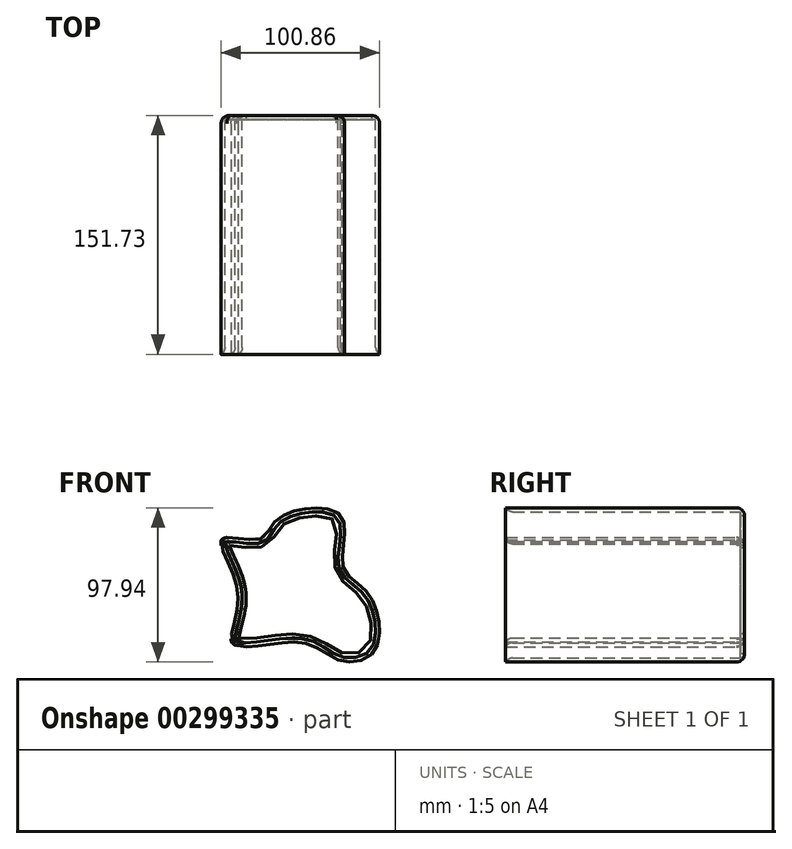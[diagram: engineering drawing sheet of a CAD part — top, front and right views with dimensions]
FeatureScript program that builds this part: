
annotation { "Feature Type Name" : "Feature", "Feature Type Description" : "" }
export const myFeature = defineFeature(function(context is Context, id is Id, definition is map)
    precondition{}
    {
        {
            var Q0;
            Q0=qCreatedBy(makeId("Front.planeOp"),FACE);
            var sketch = newSketch(context, id + "F0", { "sketchPlane" : qUnion([Q0])});
            skPoint(sketch, "E0.visualSharp", {"position": v(-34.96, 47.7) * mm});
            skPoint(sketch, "E1.visualSharp", {"position": v(-34.96, -28.37) * mm});
            skPoint(sketch, "E2.visualSharp", {"position": v(50.56, -28.37) * mm});
            skPoint(sketch, "E3.visualSharp", {"position": v(50.56, 47.7) * mm});
            skPoint(sketch, "E4.1.internal.snap0", {"position": v(-27.52, 40.25) * mm});
            skPoint(sketch, "E4.2.internal.snap0", {"position": v(-27.52, 40.25) * mm});
            skPoint(sketch, "E4.3.internal.snap0", {"position": v(-27.52, 40.25) * mm});
            skFitSpline(sketch, "E4", {"points": [v(-2.69, 52.85) * mm, v(-13.45, 40.25) * mm, v(-37.65, 40.25) * mm, v(-27.52, 5.51) * mm, v(-30.66, -26.5) * mm, v(12.64, -25.41) * mm, v(36.84, -36.71) * mm, v(59.44, -30.26) * mm, v(54.86, 6.05) * mm, v(39, 23) * mm, v(37.38, 55.54) * mm, v(-2.69, 52.85) * mm]});
            skSolve(sketch);
        }
        {
            var Q0;
            Q0=makeQuery(id+"F0.imprint","IMPRINT",FACE,{"disambiguationData":[TD([[makeQuery(id+"F0.imprint","IMPRINT",EDGE,{"derivedFrom":sQuery(id+"F0.wireOp",EDGE,"E4")}),1.0]])]});
            extrude(context, id + "F1", {"entities" : qUnion([Q0]), "depth" : 152.4 * mm});
        }
        {
            var Q0;
            Q0=makeQuery(id+"F1.opExtrude","CAP_FACE",FACE,{"disambiguationData":[OSD([sQuery(id+"F0.wireOp",EDGE,"E4")])],"isStart":false});
            shell(context, id + "F2", {"entities" : qUnion([Q0]), "thickness" : 2.54 * mm});
        }
        {
            var Q0;
            {var subQ0=sQuery(id+"F0.wireOp",EDGE,"E4");Q0=makeQuery(id+"F2.opShell","OFFSET_EDGE",EDGE,{"disambiguationData":[OSD([subQ0]),TDD([makeQuery(id+"F1.opExtrude","CAP_EDGE",EDGE,{"disambiguationData":[OSD([subQ0])],"isStart":false})]),OD(0.0)]});}
            var Q1;
            Q1=makeQuery(id+"F1.opExtrude","CAP_EDGE",EDGE,{"disambiguationData":[OSD([sQuery(id+"F0.wireOp",EDGE,"E4")])],"isStart":true});
            var Q2;
            {var subQ0=sQuery(id+"F0.wireOp",EDGE,"E4");Q2=makeQuery(id+"F2.opShell","OFFSET_EDGE",EDGE,{"disambiguationData":[OSD([subQ0]),TDD([makeQuery(id+"F1.opExtrude","CAP_EDGE",EDGE,{"disambiguationData":[OSD([subQ0])],"isStart":false})]),OD(1.0)]});}
            fillet(context, id + "F3", {"entities" : qUnion([Q0, Q1, Q2]), "radius" : 5.08 * mm, "tangentPropagation" : true, "allowEdgeOverflow" : false});
        }
        {
            var Q0;
            Q0=makeQuery(id+"F1.opExtrude","CAP_FACE",FACE,{"disambiguationData":[OSD([sQuery(id+"F0.wireOp",EDGE,"E4")])],"isStart":true});
            extrude(context, id + "F4", {"entities" : qUnion([Q0]), "operationType" : NewBodyOperationType.REMOVE, "endBound" : BoundingType.THROUGH_ALL, "oppositeDirection" : true, "depth" : 25.4 * mm});
        }
    });
